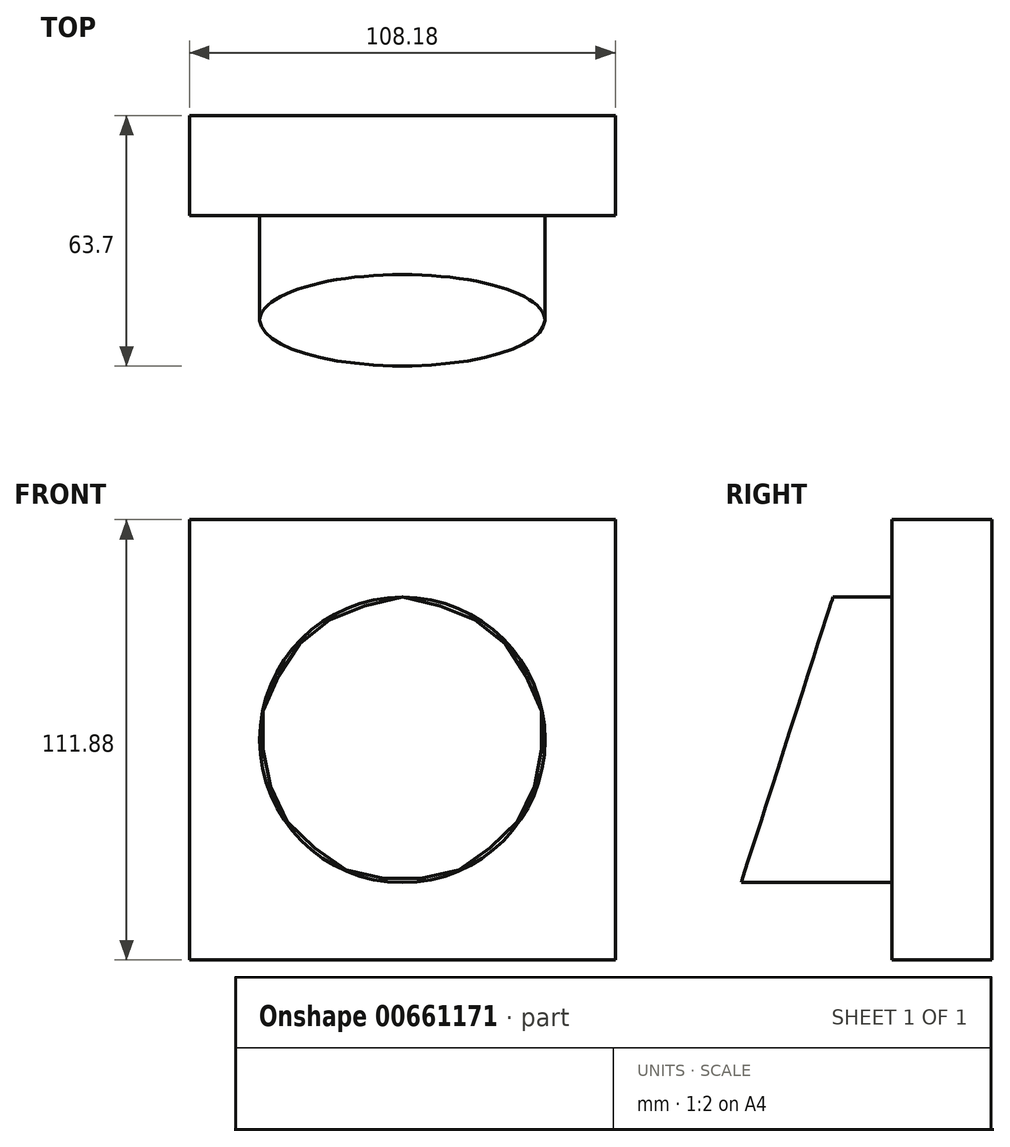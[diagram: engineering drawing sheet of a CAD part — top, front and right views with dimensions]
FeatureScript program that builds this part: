
annotation { "Feature Type Name" : "Feature", "Feature Type Description" : "" }
export const myFeature = defineFeature(function(context is Context, id is Id, definition is map)
    precondition{}
    {
        {
            var Q0;
            Q0=qCreatedBy(makeId("Front.planeOp"),FACE);
            var sketch = newSketch(context, id + "F0", { "sketchPlane" : qUnion([Q0])});
            skLineSegment(sketch, "E0.bottom", {"start": v(54.1, -55.94) * mm, "end": v(-54.1, -55.94) * mm});
            skLineSegment(sketch, "E0.top", {"start": v(54.1, 55.94) * mm, "end": v(-54.1, 55.94) * mm});
            skLineSegment(sketch, "E0.left", {"start": v(54.1, -55.94) * mm, "end": v(54.1, 55.94) * mm});
            skLineSegment(sketch, "E0.right", {"start": v(-54.1, -55.94) * mm, "end": v(-54.1, 55.94) * mm});
            skPoint(sketch, "E0.middle", {"position": v(0, 0) * mm});
            skSolve(sketch);
        }
        {
            var Q0;
            Q0=qSketchRegion(id+"F0",true);
            extrude(context, id + "F1", {"entities" : qUnion([Q0]), "depth" : 25.4 * mm, "offsetDistance" : 25.4 * mm});
        }
        {
            var Q0;
            Q0=makeQuery(id+"F1.opExtrude","CAP_FACE",FACE,{"disambiguationData":[OSD([sQuery(id+"F0.wireOp",EDGE,"E0.bottom"),sQuery(id+"F0.wireOp",EDGE,"E0.top"),sQuery(id+"F0.wireOp",EDGE,"E0.left"),sQuery(id+"F0.wireOp",EDGE,"E0.right")])],"isStart":false});
            var sketch = newSketch(context, id + "F2", { "sketchPlane" : qUnion([Q0])});
            skCircle(sketch, "E1", {"center": v(0, 0) * mm, "radius": 36.26 * mm});
            skSolve(sketch);
        }
        {
            var Q0;
            Q0=qSketchRegion(id+"F2",true);
            extrude(context, id + "F3", {"entities" : qUnion([Q0]), "operationType" : NewBodyOperationType.ADD, "depth" : 50.8 * mm, "offsetDistance" : 25.4 * mm});
        }
        {
            var Q0;
            Q0=qCreatedBy(makeId("Right.planeOp"),FACE);
            var sketch = newSketch(context, id + "F4", { "sketchPlane" : qUnion([Q0])});
            skLineSegment(sketch, "E2", {"start": v(-76.18, 54.48) * mm, "end": v(-34.57, 54.48) * mm});
            skLineSegment(sketch, "E3", {"start": v(-34.57, 54.48) * mm, "end": v(-76.18, -75.13) * mm});
            skLineSegment(sketch, "E4.bottom", {"start": v(-76.18, 54.48) * mm, "end": v(-82.46, 54.48) * mm});
            skLineSegment(sketch, "E4.top", {"start": v(-76.18, -75.28) * mm, "end": v(-82.46, -75.28) * mm});
            skLineSegment(sketch, "E4.left", {"start": v(-76.18, -75.13) * mm, "end": v(-76.18, -75.28) * mm});
            skLineSegment(sketch, "E4.right", {"start": v(-82.46, 54.48) * mm, "end": v(-82.46, -75.28) * mm});
            skSolve(sketch);
        }
        {
            var Q0;
            Q0=qSketchRegion(id+"F4",true);
            extrude(context, id + "F5", {"entities" : qUnion([Q0]), "operationType" : NewBodyOperationType.REMOVE, "endBound" : BoundingType.SYMMETRIC, "oppositeDirection" : true, "depth" : 109.47 * mm, "offsetDistance" : 25.4 * mm});
        }
    });
